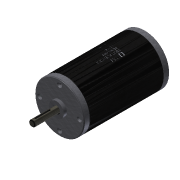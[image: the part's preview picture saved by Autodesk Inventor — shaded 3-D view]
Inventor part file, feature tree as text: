
AUTODESK INVENTOR PART (.ipt)
format: ipt  version: 2011 (Build 150239000, 239)  size: 470,528 bytes
history: native  units: in
note: dims shown in document units (in); Inventor stores cm internally (conversion verified against a paired STEP export)
features: sketch x20, extrude x15, projected_geometry x8, other x5, chamfer x4, plane x4, fillet x2, mirror x1, hole x1, revolve x1, pattern_circular x1
ambient origin geometry x8: Origin, YZ Plane, XZ Plane, XY Plane, X Axis, Y Axis, Z Axis, Center Point
bodies: Solid1 (feature_tree)
feature tree (62):
  extrude  "Extrusion1"  Depth=3.75in TaperAngle=0.0deg
  fillet  "Fillet1"  Radius=0.025in
  extrude  "Extrusion3"  Depth=0.035in TaperAngle=45.0deg
  mirror  "Mirror1"
  chamfer  "Chamfer1"  Distance=0.16in
  other  "Decal1"
  extrude  "Extrusion4"  Depth=4.0in TaperAngle=0.0deg
  extrude  "Extrusion5"  Depth=5.245in TaperAngle=0.0deg
  extrude  "Extrusion6"  TaperAngle=180.0deg  [1 undecoded]
  chamfer  "Chamfer2"  Distance=0.05in
  plane  "Work Plane1"
  extrude  "Extrusion7"  Depth=0.1815in TaperAngle=0.0deg
  extrude  "Extrusion8"  Depth=0.075in TaperAngle=45.0deg
  fillet  "Fillet2"  Radius=1.0in
  chamfer  "Chamfer3"  Distance=1.5748in Angle=360.0deg
  hole  "Hole1"  [1 undecoded]
  extrude  "Extrusion9"  Depth=0.404in
  plane  "Work Plane3"
  sketch  "Sketch11"  dims[d44=180.0deg]
  extrude  "Extrusion10"  TaperAngle=0.0deg  [1 undecoded]
  extrude  "Extrusion11"  Depth=1.987in
  extrude  "Extrusion12"  Depth=4.125in TaperAngle=0.0deg
  extrude  "Extrusion13"  Depth=0.375in TaperAngle=0.0deg
  extrude  "Extrusion14"  Depth=0.404in
  extrude  "Extrusion15"  TaperAngle=0.0deg  [1 undecoded]
  chamfer  "Chamfer4"  Distance=0.9935in
  plane  "Work Plane4"
  revolve  "Revolution1"  Angle=360.0deg
  extrude  "Extrusion16"  Depth=0.25in TaperAngle=0.0deg
  pattern_circular  "Circular Pattern1"  [2 undecoded]
  sketch  "Sketch20"  dims[d87=0.9935in d88=4.125in d89=0.0in d90=0.375in d91=0.0in d92=0.404in d93=0.0in d94=0.9935in d95=0.7874in d97=360.0deg d99=0.25in d100=0.0in d101=1.987in d102=0.125in d103=0.125in d104=3.875in d105=0.0in d106=0.409in d107=0.25in d108=0.22in d109=0.252in d110=0.314in d111=0.314in d112=0.096in d113=0.0in d114=0.144in d115=0.125in d116=0.0in d117=0.085in d118=0.125in d119=45.0deg d120=0.136in d121=0.136in d122=0.134in d123=90.0deg d124=0.075in d125=0.075in d126=0.0375in d127=0.0375in d128=0.125in d129=0.125in d130=0.125in d131=0.125in d132=0.1in d133=-0.2199in d134=0.7874in d135=360.0deg]
  sketch  "Sketch1"  dims[d0=2.5in d1=3.75in d2=0.0in d3=0.025in]
  sketch  "Sketch2"  dims[d7=0.287in d8=0.0in d9=0.035in d10=0.125in d11=45.0deg]
  projected_geometry  "Projected Loop1"
  sketch  "Sketch3"  dims[d21=1.3in]
  other  "Image1"
  projected_geometry  "Projected Loop2"
  sketch  "Sketch4"  dims[d22=1.1in]
  sketch  "Sketch5"  dims[d27=0.6in]
  sketch  "Sketch6"  dims[d28=0.75in d29=0.16in d30=0.0in]
  sketch  "Sketch7"  dims[d31=0.375in d32=4.0in d33=0.0in]
  sketch  "Sketch8"  dims[d35=0.3125in d36=5.245in d37=0.0in]
  sketch  "Sketch9"  dims[d39=0.04in d40=0.125in d41=45.0deg d42=180.0deg]
  projected_geometry  "Projected Loop3"
  sketch  "Sketch10"  dims[d43=0.075in]
  projected_geometry  "Projected Loop4"
  projected_geometry  "Projected Loop5"
  projected_geometry  "Projected Loop6"
  other  "Work Axis1"
  plane  "Work Plane2"
  sketch  "Sketch12"  dims[d45=0.7925in]
  sketch  "Sketch13"  dims[d46=0.185in d47=0.05in d48=0.0in]
  sketch  "Sketch14"  dims[d49=1.176in d50=0.1815in d51=0.0in]
  sketch  "Sketch15"  dims[d52=0.0125in d53=0.075in d54=0.125in d55=45.0deg d56=1.0in d57=1.5748in d59=360.0deg]
  sketch  "Sketch16"  dims[d61=0.13in d62=0.5in d63=0.25in d64=0.25in d65=0.5635in d66=0.5in d67=0.0in d68=0.425in d69=0.0in]
  sketch  "Sketch17"  dims[d71=90.0deg d82=0.404in]
  projected_geometry  "Projected Loop7"
  projected_geometry  "Projected Loop8"
  other  "Work Axis2"
  other  "Work Axis3"
  sketch  "Sketch18"  dims[d83=0.404in d84=0.0in]
  sketch  "Sketch19"  dims[d85=0.0in d86=1.987in]
note: 6 required parameter values undecoded (feature->parameter linkage not recoverable at this tier; creation-order binding heuristic only, values carry confidence <= 0.55)
